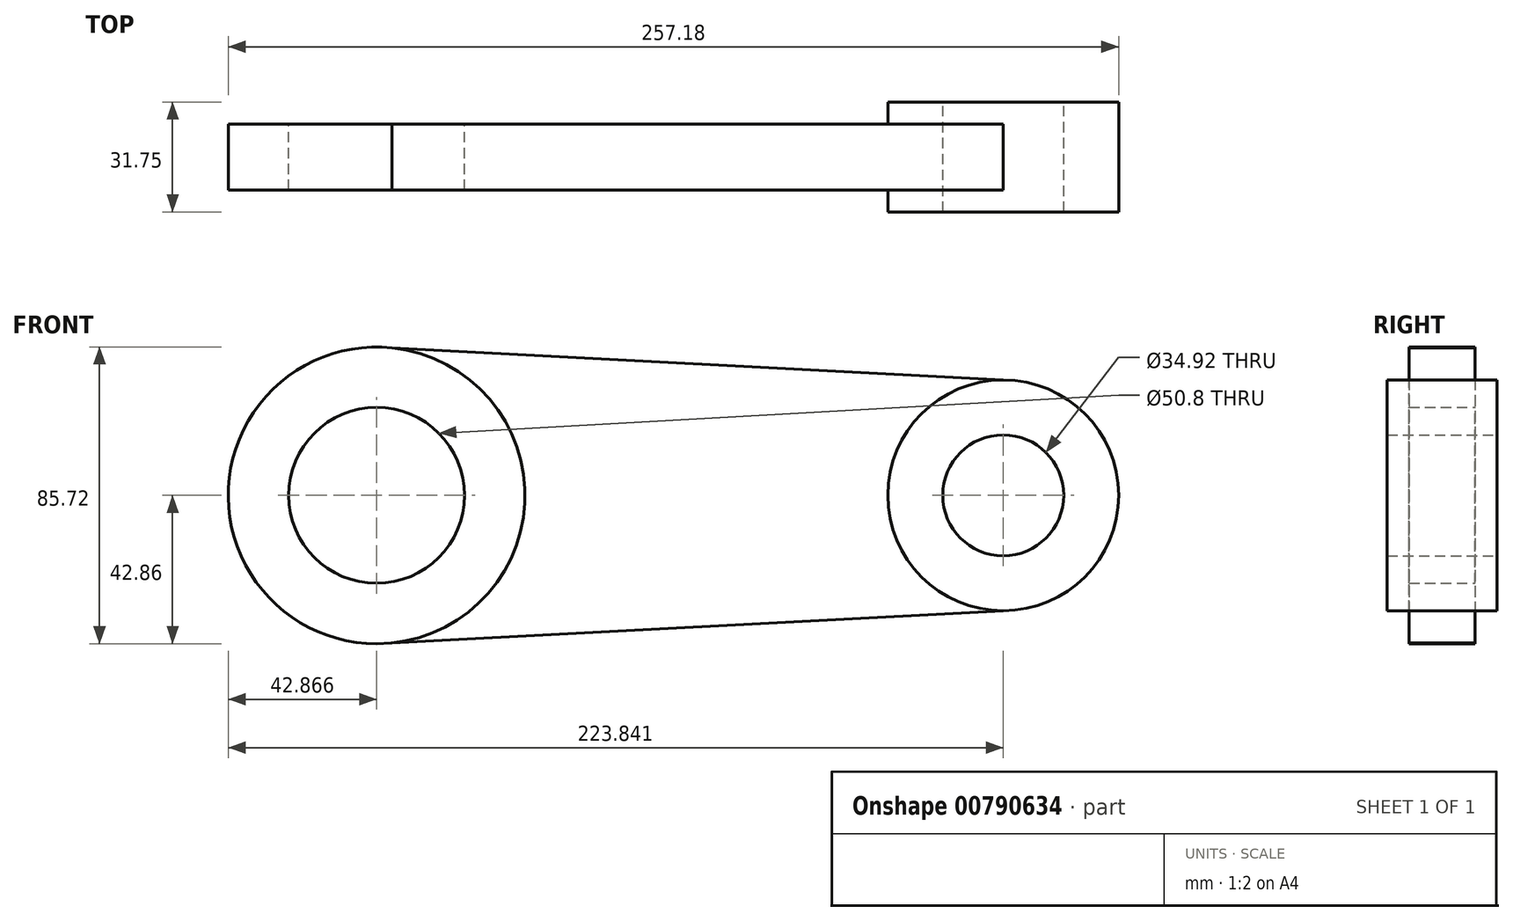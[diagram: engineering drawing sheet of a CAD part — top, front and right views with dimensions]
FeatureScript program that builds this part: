
annotation { "Feature Type Name" : "Feature", "Feature Type Description" : "" }
export const myFeature = defineFeature(function(context is Context, id is Id, definition is map)
    precondition{}
    {
        {
            var Q0;
            Q0=qCreatedBy(makeId("Front.planeOp"),FACE);
            var sketch = newSketch(context, id + "F0", { "sketchPlane" : qUnion([Q0])});
            skLineSegment(sketch, "E0", {"start": v(147, 0) * mm, "end": v(-33.98, 0) * mm, "construction": true});
            skCircle(sketch, "E1", {"center": v(-33.98, 0) * mm, "radius": 25.4 * mm});
            skCircle(sketch, "E2", {"center": v(-33.98, 0) * mm, "radius": 42.86 * mm});
            skCircle(sketch, "E3", {"center": v(147, 0) * mm, "radius": 17.46 * mm});
            skCircle(sketch, "E4", {"center": v(147, 0) * mm, "radius": 33.34 * mm});
            skLineSegment(sketch, "E5", {"start": v(-33.98, 0) * mm, "end": v(-33.98, 42.86) * mm, "construction": true});
            skLineSegment(sketch, "E6", {"start": v(-33.98, 0) * mm, "end": v(-33.98, -42.86) * mm, "construction": true});
            skLineSegment(sketch, "E7", {"start": v(147, 0) * mm, "end": v(147, 33.34) * mm, "construction": true});
            skLineSegment(sketch, "E8", {"start": v(147, 0) * mm, "end": v(147, -33.34) * mm, "construction": true});
            skLineSegment(sketch, "E9", {"start": v(-33.98, -42.86) * mm, "end": v(147, -33.34) * mm});
            skLineSegment(sketch, "E10", {"start": v(-33.98, 42.86) * mm, "end": v(147, 33.34) * mm});
            skSolve(sketch);
        }
        {
            var Q0;
            Q0 = qSketchRegion(id + "F0", true);
            extrude(context, id + "F1", {"entities" : qUnion([Q0]), "depth" : 19.05 * mm, "offsetDistance" : 25.4 * mm});
        }
        {
            var Q0;
            Q0=makeQuery(id+"F1.opExtrude","CAP_FACE",FACE,{"disambiguationData":[OSD([sQuery(id+"F0.wireOp",EDGE,"E1"),sQuery(id+"F0.wireOp",EDGE,"E2"),sQuery(id+"F0.wireOp",EDGE,"E3"),sQuery(id+"F0.wireOp",EDGE,"E4"),sQuery(id+"F0.wireOp",EDGE,"E9"),sQuery(id+"F0.wireOp",EDGE,"E10")])],"isStart":false});
            var sketch = newSketch(context, id + "F2", { "sketchPlane" : qUnion([Q0])});
            skLineSegment(sketch, "E11", {"start": v(0, 0) * mm, "end": v(-33.98, 0) * mm, "construction": true});
            skLineSegment(sketch, "E12", {"start": v(-33.98, 0) * mm, "end": v(147, 0) * mm, "construction": true});
            skCircle(sketch, "E13", {"center": v(-33.98, 0) * mm, "radius": 42.86 * mm});
            skCircle(sketch, "E14", {"center": v(147, 0) * mm, "radius": 33.34 * mm});
            skSolve(sketch);
        }
        {
            var Q0;
            Q0=makeQuery(id+"F2.imprint","IMPRINT",FACE,{"disambiguationData":[TD([[makeQuery(id+"F2.imprint","IMPRINT",EDGE,{"derivedFrom":makeQuery(id+"F1.opExtrude","CAP_EDGE",EDGE,{"disambiguationData":[OSD([sQuery(id+"F0.wireOp",EDGE,"E1")])],"isStart":false})}),-1.0]])]});
            extrude(context, id + "F3", {"entities" : qUnion([Q0]), "operationType" : NewBodyOperationType.ADD, "depth" : 5 / 203.2 * mm, "offsetDistance" : 25.4 * mm});
        }
        {
            var Q0;
            Q0=makeQuery(id+"F1.opExtrude","CAP_FACE",FACE,{"disambiguationData":[OSD([sQuery(id+"F0.wireOp",EDGE,"E1"),sQuery(id+"F0.wireOp",EDGE,"E2"),sQuery(id+"F0.wireOp",EDGE,"E3"),sQuery(id+"F0.wireOp",EDGE,"E4"),sQuery(id+"F0.wireOp",EDGE,"E9"),sQuery(id+"F0.wireOp",EDGE,"E10")])],"isStart":false});
            var sketch = newSketch(context, id + "F4", { "sketchPlane" : qUnion([Q0])});
            skLineSegment(sketch, "E15", {"start": v(0, 0) * mm, "end": v(147, 0) * mm, "construction": true});
            skCircle(sketch, "E16", {"center": v(147, 0) * mm, "radius": 33.34 * mm});
            skSolve(sketch);
        }
        {
            var Q0;
            Q0=makeQuery(id+"F4.imprint","IMPRINT",FACE,{"disambiguationData":[TD([[makeQuery(id+"F4.imprint","IMPRINT",EDGE,{"derivedFrom":makeQuery(id+"F1.opExtrude","CAP_EDGE",EDGE,{"disambiguationData":[OSD([sQuery(id+"F0.wireOp",EDGE,"E3")])],"isStart":false})}),-1.0]])]});
            extrude(context, id + "F5", {"entities" : qUnion([Q0]), "operationType" : NewBodyOperationType.ADD, "depth" : 6.35 * mm, "offsetDistance" : 25.4 * mm});
        }
        {
            var Q0;
            Q0=makeQuery(id+"F1.opExtrude","CAP_FACE",FACE,{"disambiguationData":[OSD([sQuery(id+"F0.wireOp",EDGE,"E1"),sQuery(id+"F0.wireOp",EDGE,"E2"),sQuery(id+"F0.wireOp",EDGE,"E3"),sQuery(id+"F0.wireOp",EDGE,"E4"),sQuery(id+"F0.wireOp",EDGE,"E9"),sQuery(id+"F0.wireOp",EDGE,"E10")])],"isStart":true});
            var sketch = newSketch(context, id + "F6", { "sketchPlane" : qUnion([Q0])});
            skLineSegment(sketch, "E17", {"start": v(0, 0) * mm, "end": v(33.98, 0) * mm, "construction": true});
            skLineSegment(sketch, "E18", {"start": v(33.98, 0) * mm, "end": v(-147, 0) * mm, "construction": true});
            skCircle(sketch, "E19", {"center": v(-147, 0) * mm, "radius": 33.34 * mm});
            skCircle(sketch, "E20", {"center": v(33.98, 0) * mm, "radius": 42.86 * mm});
            skSolve(sketch);
        }
        {
            var Q0;
            {var subQ0=sQuery(id+"F6.wireOp",EDGE,"E19");Q0=makeQuery(id+"F6.imprint","IMPRINT",FACE,{"disambiguationData":[TD([[makeQuery(id+"F6.imprint","IMPRINT",EDGE,{"disambiguationData":[OD(0.0)],"derivedFrom":subQ0}),-1.0]])]});}
            extrude(context, id + "F7", {"entities" : qUnion([Q0]), "operationType" : NewBodyOperationType.ADD, "depth" : 6.35 * mm, "offsetDistance" : 25.4 * mm});
        }
        {
            var Q0;
            Q0=makeQuery(id+"F1.opExtrude","CAP_FACE",FACE,{"disambiguationData":[OSD([sQuery(id+"F0.wireOp",EDGE,"E1"),sQuery(id+"F0.wireOp",EDGE,"E2"),sQuery(id+"F0.wireOp",EDGE,"E3"),sQuery(id+"F0.wireOp",EDGE,"E4"),sQuery(id+"F0.wireOp",EDGE,"E9"),sQuery(id+"F0.wireOp",EDGE,"E10")])],"isStart":true});
            var sketch = newSketch(context, id + "F8", { "sketchPlane" : qUnion([Q0])});
            skLineSegment(sketch, "E21", {"start": v(0, 0) * mm, "end": v(33.98, 0) * mm, "construction": true});
            skCircle(sketch, "E22", {"center": v(33.98, 0) * mm, "radius": 42.86 * mm});
            skSolve(sketch);
        }
        {
            var Q0;
            {var subQ0=sQuery(id+"F8.wireOp",EDGE,"E22");Q0=makeQuery(id+"F8.imprint","IMPRINT",FACE,{"disambiguationData":[TD([[makeQuery(id+"F8.imprint","IMPRINT",EDGE,{"disambiguationData":[OD(0.0)],"derivedFrom":subQ0}),-1.0]])]});}
            extrude(context, id + "F9", {"entities" : qUnion([Q0]), "operationType" : NewBodyOperationType.ADD, "depth" : 5 / 203.2 * mm, "offsetDistance" : 25.4 * mm});
        }
    });
